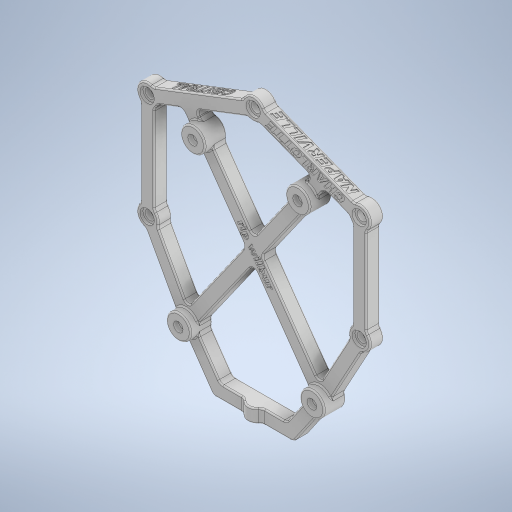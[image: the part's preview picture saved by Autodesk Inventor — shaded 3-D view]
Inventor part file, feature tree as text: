
AUTODESK INVENTOR PART (.ipt)
format: ipt  version: 2024.2 (Build 282272000, 272)  size: 2,070,016 bytes
history: native  units: mm
features: projected_geometry x126, reference x43, sketch x11, extrude x7, other x5, fillet x4, emboss x4, hole x3, plane x1
ambient origin geometry x8: Origin, YZ Plane, XZ Plane, XY Plane, X Axis, Y Axis, Z Axis, Center Point
bodies: Solid1 (feature_tree)
feature tree (204):
  plane  "Work Plane1"
  extrude  "Extrusion1"  Depth=49.0mm
  extrude  "Extrusion4"  Depth=5.25mm
  sketch  "Sketch2"  dims[d2=62.0mm d3=5.25mm]
  extrude  "Extrusion2"  Depth=18.0mm
  extrude  "Extrusion3"  Depth=2.5mm
  hole  "Hole1"  [1 undecoded]
  hole  "Hole2"  [1 undecoded]
  sketch  "Sketch6"  dims[d10=2.5mm d11=2.5mm]
  extrude  "Extrusion5"  Depth=5.000004mm
  hole  "Hole3"  [1 undecoded]
  fillet  "Fillet1"  Radius=1.9mm
  fillet  "Fillet2"  Radius=6.0mm
  fillet  "Fillet3"  Radius=3.0mm
  fillet  "Fillet4"  Radius=2.0mm
  emboss  "Emboss1"
  emboss  "Emboss2"
  sketch  "Sketch10"  dims[d26=3.5mm d27=6.0mm d28=4.0mm d29=2.0mm d30=90.0deg d31=1.0mm d32=0.0mm]
  emboss  "Emboss4"
  emboss  "Emboss5"
  extrude  "Extrusion6"  Depth=10.0mm
  extrude  "Extrusion7"  Depth=10.0mm TaperAngle=0.0deg
  sketch  "Sketch1"  dims[d0=9.0mm d1=49.0mm]
  reference  "Reference1"
  reference  "Reference2"
  reference  "Reference3"
  reference  "Reference4"
  reference  "Reference5"
  reference  "Reference6"
  reference  "Reference7"
  reference  "Reference8"
  reference  "Reference9"
  reference  "Reference10"
  reference  "Reference11"
  reference  "Reference12"
  reference  "Reference13"
  reference  "Reference14"
  reference  "Reference15"
  reference  "Reference16"
  reference  "Reference17"
  reference  "Reference18"
  reference  "Reference19"
  reference  "Reference20"
  reference  "Reference21"
  reference  "Reference22"
  reference  "Reference23"
  reference  "Reference24"
  reference  "Reference25"
  reference  "Reference26"
  reference  "Reference27"
  reference  "Reference28"
  reference  "Reference29"
  reference  "Reference30"
  reference  "Reference31"
  reference  "Reference32"
  reference  "Reference33"
  reference  "Reference34"
  reference  "Reference35"
  reference  "Reference36"
  reference  "Reference37"
  reference  "Reference38"
  reference  "Reference39"
  reference  "Reference40"
  reference  "Reference41"
  reference  "Reference42"
  reference  "Reference43"
  sketch  "Sketch3"  dims[d4=5.25mm d5=18.0mm]
  sketch  "Sketch4"  dims[d6=5.0mm d7=2.5mm]
  sketch  "Sketch5"  dims[d8=2.5mm d9=5.0mm]
  projected_geometry  "Projected Loop1"
  projected_geometry  "Projected Loop2"
  projected_geometry  "Projected Loop3"
  projected_geometry  "Projected Loop4"
  projected_geometry  "Projected Loop5"
  projected_geometry  "Projected Loop6"
  projected_geometry  "Projected Loop7"
  projected_geometry  "Projected Loop8"
  projected_geometry  "Projected Loop9"
  projected_geometry  "Projected Loop10"
  projected_geometry  "Projected Loop11"
  projected_geometry  "Projected Loop12"
  projected_geometry  "Projected Loop13"
  projected_geometry  "Projected Loop14"
  projected_geometry  "Projected Loop15"
  projected_geometry  "Projected Loop16"
  projected_geometry  "Projected Loop17"
  projected_geometry  "Projected Loop18"
  projected_geometry  "Projected Loop19"
  projected_geometry  "Projected Loop20"
  projected_geometry  "Projected Loop21"
  projected_geometry  "Projected Loop22"
  projected_geometry  "Projected Loop23"
  projected_geometry  "Projected Loop24"
  projected_geometry  "Projected Loop25"
  projected_geometry  "Projected Loop26"
  projected_geometry  "Projected Loop27"
  projected_geometry  "Projected Loop28"
  projected_geometry  "Projected Loop29"
  projected_geometry  "Projected Loop30"
  projected_geometry  "Projected Loop31"
  projected_geometry  "Projected Loop32"
  projected_geometry  "Projected Loop33"
  projected_geometry  "Projected Loop34"
  projected_geometry  "Projected Loop35"
  projected_geometry  "Projected Loop36"
  projected_geometry  "Projected Loop37"
  projected_geometry  "Projected Loop38"
  projected_geometry  "Projected Loop39"
  projected_geometry  "Projected Loop40"
  projected_geometry  "Projected Loop41"
  projected_geometry  "Projected Loop42"
  projected_geometry  "Projected Loop43"
  projected_geometry  "Projected Loop44"
  projected_geometry  "Projected Loop45"
  projected_geometry  "Projected Loop46"
  projected_geometry  "Projected Loop47"
  projected_geometry  "Projected Loop48"
  projected_geometry  "Projected Loop49"
  projected_geometry  "Projected Loop50"
  projected_geometry  "Projected Loop51"
  projected_geometry  "Projected Loop52"
  projected_geometry  "Projected Loop53"
  projected_geometry  "Projected Loop54"
  projected_geometry  "Projected Loop55"
  projected_geometry  "Projected Loop56"
  projected_geometry  "Projected Loop57"
  projected_geometry  "Projected Loop58"
  projected_geometry  "Projected Loop59"
  projected_geometry  "Projected Loop60"
  projected_geometry  "Projected Loop61"
  projected_geometry  "Projected Loop62"
  projected_geometry  "Projected Loop63"
  projected_geometry  "Projected Loop64"
  projected_geometry  "Projected Loop65"
  projected_geometry  "Projected Loop66"
  projected_geometry  "Projected Loop67"
  projected_geometry  "Projected Loop68"
  projected_geometry  "Projected Loop69"
  projected_geometry  "Projected Loop70"
  projected_geometry  "Projected Loop71"
  projected_geometry  "Projected Loop72"
  projected_geometry  "Projected Loop73"
  projected_geometry  "Projected Loop74"
  projected_geometry  "Projected Loop75"
  projected_geometry  "Projected Loop76"
  projected_geometry  "Projected Loop77"
  projected_geometry  "Projected Loop78"
  projected_geometry  "Projected Loop79"
  projected_geometry  "Projected Loop80"
  projected_geometry  "Projected Loop81"
  projected_geometry  "Projected Loop82"
  projected_geometry  "Projected Loop83"
  projected_geometry  "Projected Loop84"
  projected_geometry  "Projected Loop85"
  projected_geometry  "Projected Loop86"
  projected_geometry  "Projected Loop87"
  projected_geometry  "Projected Loop88"
  projected_geometry  "Projected Loop89"
  projected_geometry  "Projected Loop90"
  projected_geometry  "Projected Loop91"
  projected_geometry  "Projected Loop92"
  projected_geometry  "Projected Loop93"
  projected_geometry  "Projected Loop94"
  projected_geometry  "Projected Loop95"
  projected_geometry  "Projected Loop96"
  projected_geometry  "Projected Loop97"
  projected_geometry  "Projected Loop98"
  projected_geometry  "Projected Loop99"
  projected_geometry  "Projected Loop100"
  projected_geometry  "Projected Loop101"
  projected_geometry  "Projected Loop102"
  projected_geometry  "Projected Loop103"
  projected_geometry  "Projected Loop104"
  projected_geometry  "Projected Loop105"
  projected_geometry  "Projected Loop106"
  projected_geometry  "Projected Loop107"
  projected_geometry  "Projected Loop108"
  projected_geometry  "Projected Loop109"
  projected_geometry  "Projected Loop110"
  projected_geometry  "Projected Loop111"
  projected_geometry  "Projected Loop112"
  projected_geometry  "Projected Loop113"
  projected_geometry  "Projected Loop114"
  projected_geometry  "Projected Loop115"
  projected_geometry  "Projected Loop116"
  projected_geometry  "Projected Loop117"
  projected_geometry  "Projected Loop118"
  projected_geometry  "Projected Loop119"
  projected_geometry  "Projected Loop120"
  projected_geometry  "Projected Loop121"
  projected_geometry  "Projected Loop122"
  projected_geometry  "Projected Loop123"
  projected_geometry  "Projected Loop124"
  projected_geometry  "Projected Loop125"
  projected_geometry  "Projected Loop126"
  sketch  "Sketch7"  dims[d14=2.5mm d15=5.000004mm]
  sketch  "Sketch8"  dims[d17=5.6mm d18=5.0mm d19=0.0mm d20=1.9mm d21=0.0mm d22=6.0mm d23=0.0mm d24=3.0mm d25=0.0mm]
  sketch  "Sketch11"  dims[d33=5.25mm d34=6.0mm d35=4.0mm d36=2.0mm d37=90.0deg d38=1.0mm d39=0.0mm d40=2.0mm]
  sketch  "Sketch12"  dims[d41=1.5mm d42=7.0mm d43=3.0mm d44=0.0mm d45=2.8mm d46=6.0mm d47=4.0mm d48=2.0mm d49=90.0deg d50=4.0mm d51=0.0mm d52=0.5mm d53=0.5mm d54=96.0mm d55=5.0mm d56=2.5mm d57=2.5mm d58=5.0mm d60=10.0mm d61=2.5mm d62=2.5mm d63=2.5mm d64=2.5mm d65=2.5mm d66=5.0mm d67=27.0mm d68=0.35mm d69=0.0mm d70=0.35mm d71=0.0mm d74=0.35mm d75=0.0mm d76=0.35mm d77=0.0mm d78=0.2mm d79=0.0mm d80=0.2mm d81=0.0mm]
  other  "<userpath>\Desktop\scioly-robot-tour\Hardware\ipt\v3\v3.iam"
  other  "v3.iam"
  other  "v3chassis:1"
  other  "<userpath>\Desktop\scioly-robot-tour\Hardware\ipt\v3\v2.iam"
  other  "v2.iam"
note: 3 required parameter values undecoded (feature->parameter linkage not recoverable at this tier; creation-order binding heuristic only, values carry confidence <= 0.55)
